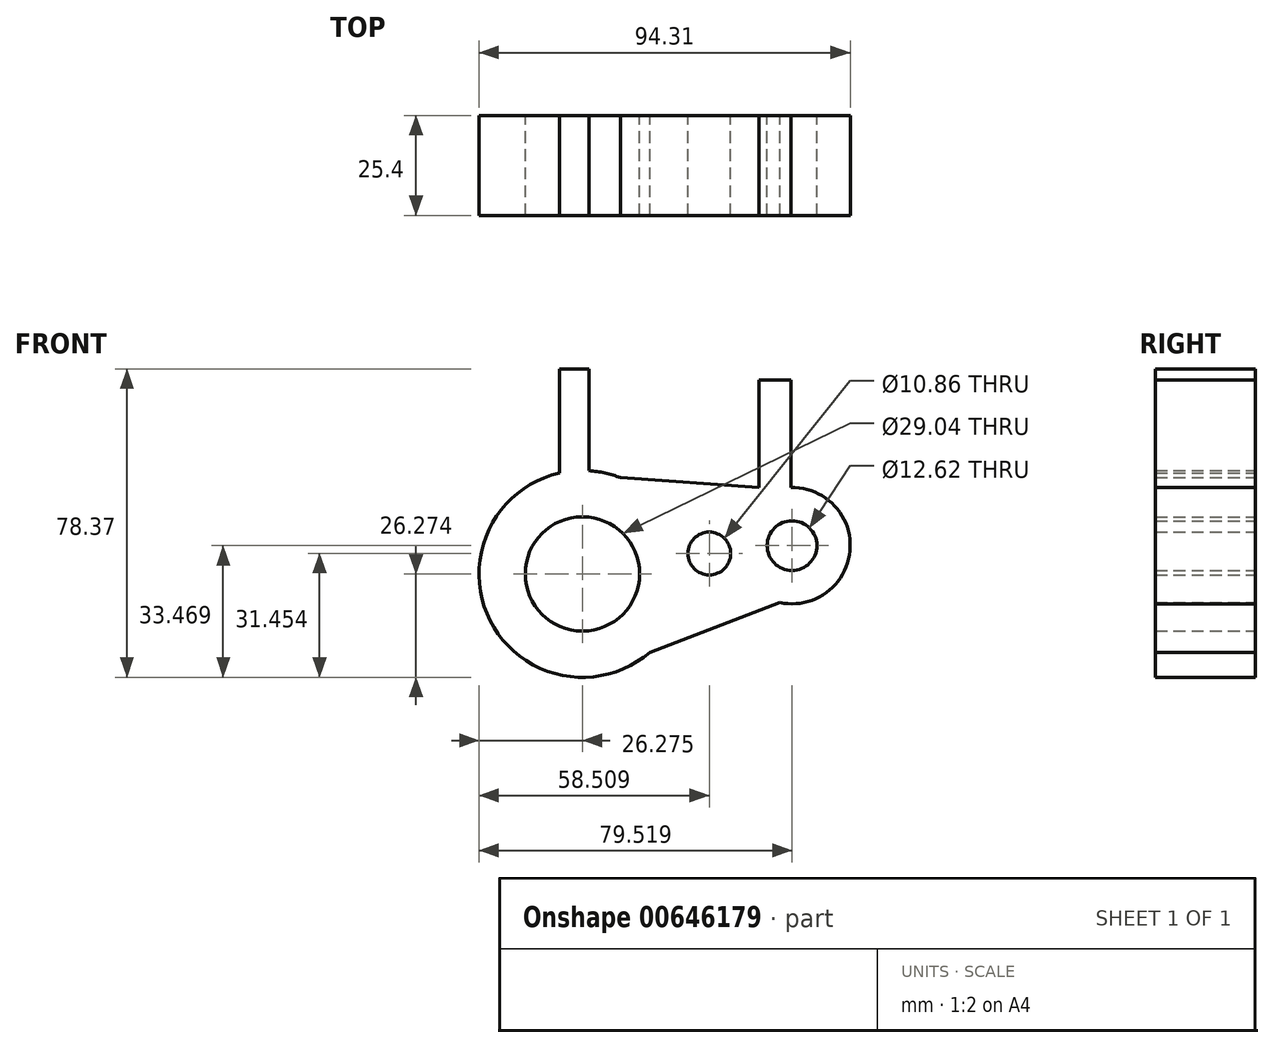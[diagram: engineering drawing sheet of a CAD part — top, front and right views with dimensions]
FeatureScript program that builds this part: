
annotation { "Feature Type Name" : "Feature", "Feature Type Description" : "" }
export const myFeature = defineFeature(function(context is Context, id is Id, definition is map)
    precondition{}
    {
        {
            var Q0;
            Q0=qCreatedBy(makeId("Front.planeOp"),FACE);
            var sketch = newSketch(context, id + "F0", { "sketchPlane" : qUnion([Q0])});
            skCircle(sketch, "E0", {"center": v(-39.29, 11.94) * mm, "radius": 26.27 * mm});
            skCircle(sketch, "E1", {"center": v(13.96, 19.14) * mm, "radius": 14.8 * mm});
            skLineSegment(sketch, "E2", {"start": v(-29.63, 36.38) * mm, "end": v(10.66, 33.56) * mm});
            skLineSegment(sketch, "E3", {"start": v(-22.14, -7.96) * mm, "end": v(10.84, 4.68) * mm});
            skCircle(sketch, "E4", {"center": v(-39.29, 11.94) * mm, "radius": 14.52 * mm});
            skCircle(sketch, "E5", {"center": v(13.96, 19.14) * mm, "radius": 6.31 * mm});
            skCircle(sketch, "E6", {"center": v(-7.05, 17.12) * mm, "radius": 5.43 * mm});
            skLineSegment(sketch, "E7.bottom", {"start": v(5.56, 33.92) * mm, "end": v(13.67, 33.92) * mm});
            skLineSegment(sketch, "E7.top", {"start": v(5.56, 61.16) * mm, "end": v(13.67, 61.16) * mm});
            skLineSegment(sketch, "E7.left", {"start": v(5.56, 33.92) * mm, "end": v(5.56, 61.16) * mm});
            skLineSegment(sketch, "E7.right", {"start": v(13.67, 33.92) * mm, "end": v(13.67, 61.16) * mm});
            skLineSegment(sketch, "E8.bottom", {"start": v(-45.13, 37.56) * mm, "end": v(-37.56, 37.56) * mm});
            skLineSegment(sketch, "E8.top", {"start": v(-45.13, 64.04) * mm, "end": v(-37.56, 64.04) * mm});
            skLineSegment(sketch, "E8.left", {"start": v(-45.13, 37.56) * mm, "end": v(-45.13, 64.04) * mm});
            skLineSegment(sketch, "E8.right", {"start": v(-37.56, 37.56) * mm, "end": v(-37.56, 64.04) * mm});
            skSolve(sketch);
        }
        {
            var Q0;
            Q0 = qSketchRegion(id + "F0", true);
            extrude(context, id + "F1", {"entities" : qUnion([Q0]), "depth" : 25.4 * mm, "offsetDistance" : 25.4 * mm});
        }
    });
